# Revit family: Flush_Valve-Service_Sink-Zurn-Z6017AV
name_source: partatom
category: Plumbing Fixtures
units: mm (PartAtom-declared; Revit-internal decimal feet)

## family parameters
Cut with Voids When Loaded = No
Host = Face
Maintain Annotation Orientation = No
OmniClass Number = 23.45.05.14.99
OmniClass Title = Other Sanitary Washing Plumbing Fixtures
Part Type = Normal
Room Calculation Point = No
Round Connector Dimension = Use Radius
Shared = No

## types (1)
- Z6017AV (Exposed Flush Valve for Clinic Service Sinks- 6.5 GPF, 24" R-I)
    Activation Method = Manual Operated
    Assembly Code = D2010.60
    CW Connection = Yes
    CWFU = 0
    Centerline of Stop Valve to Centerline of Flush Valve = 4.75 "
    Default Elevation = 48 "
    Description = Exposed Flush Valve for Clinic Service Sinks
    Flush Rate (GPF) = 6.5 GPF
    HW Connection = No
    HWFU = 0
    Inlet Connection Size (inch) = 1 "
    Main Material = Chrome-Plated Brass - Zurn - Polished
    Manufacturer = Zurn Water, LLC
    Manufacturer Brand = Zurn
    Max Working Water Temperature = 104 °F
    Model = Z6017AV
    Modified Date = 12/17/2025
    Operating Water Pressure (PSI) = 25 – 80 PSI (172 – 552 kPa)
    Product Documentation Link = https://files.zurn.com
    Product Installation Sheet URL = https://files.zurn.com
    Product Page URL = https://www.zurn.com
    Product data URL = https://bimobject.com
    Repair Parts URL = https://files.zurn.com
    URL = https://www.zurn.com
    Vent Connection = No
    WFU = 0
    Waste Connection = No

## geometry (parser evidence)
native form markers: Blend x4, Sweep x13
no freeform markers — native parametric forms only
